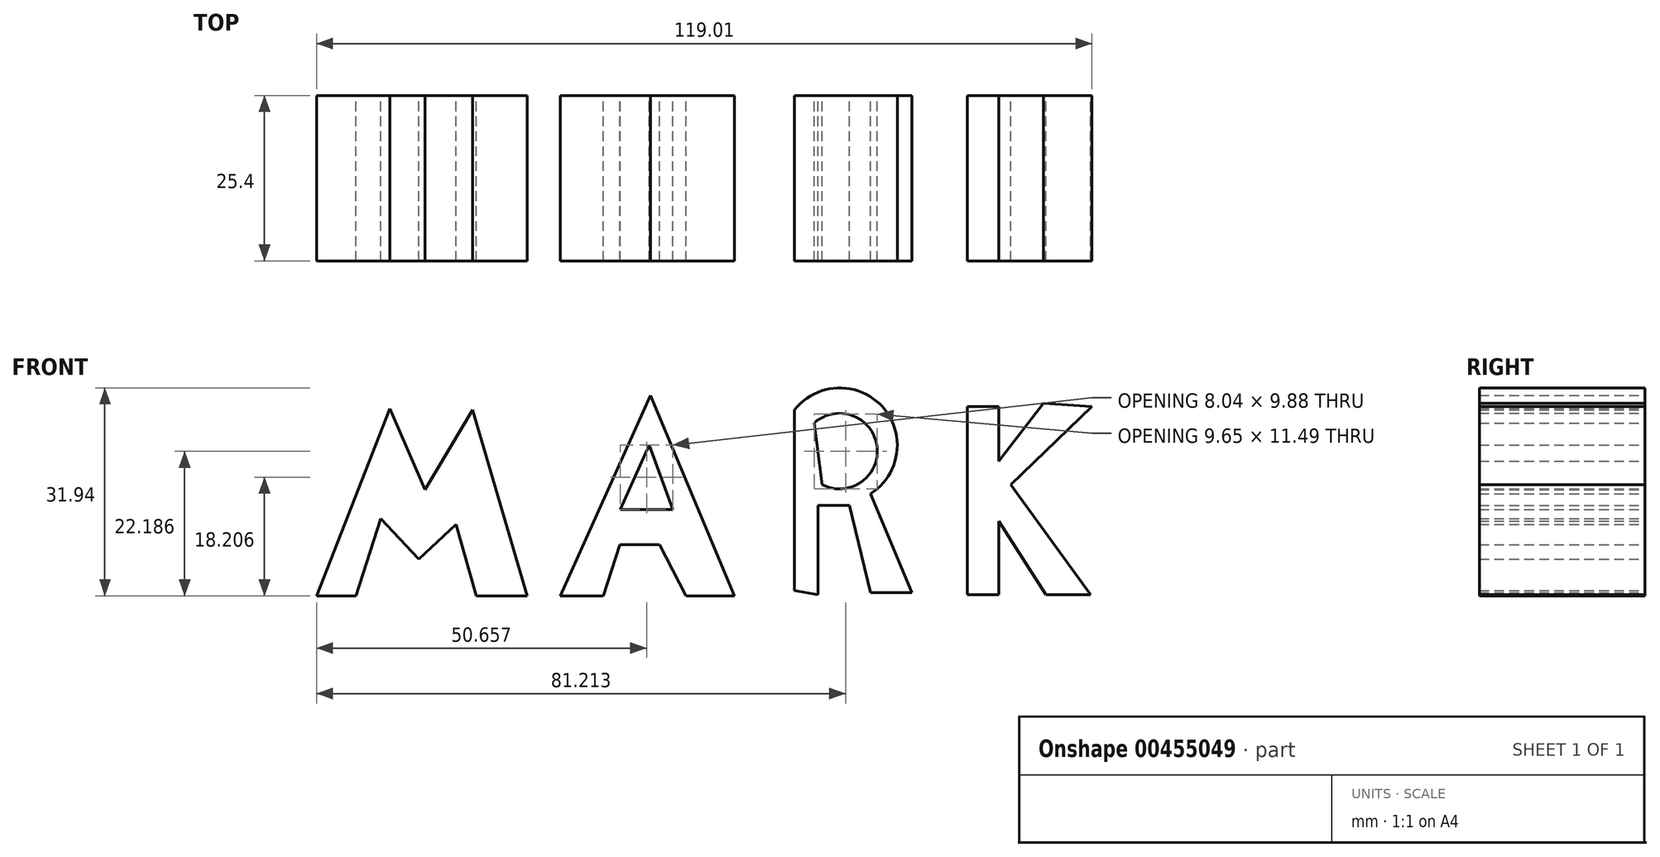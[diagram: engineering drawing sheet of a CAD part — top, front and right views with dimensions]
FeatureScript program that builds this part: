
annotation { "Feature Type Name" : "Feature", "Feature Type Description" : "" }
export const myFeature = defineFeature(function(context is Context, id is Id, definition is map)
    precondition{}
    {
        {
            var Q0;
            Q0=qCreatedBy(makeId("Front.planeOp"),FACE);
            var sketch = newSketch(context, id + "F0", { "sketchPlane" : qUnion([Q0])});
            skLineSegment(sketch, "E0", {"start": v(-68.75, -36.99) * mm, "end": v(-62.72, -36.99) * mm});
            skLineSegment(sketch, "E1", {"start": v(-62.72, -36.99) * mm, "end": v(-58.9, -25.13) * mm});
            skLineSegment(sketch, "E2", {"start": v(-58.9, -25.13) * mm, "end": v(-53.07, -31.36) * mm});
            skLineSegment(sketch, "E3", {"start": v(-53.07, -31.36) * mm, "end": v(-47.36, -26.01) * mm});
            skLineSegment(sketch, "E4", {"start": v(-47.36, -26.01) * mm, "end": v(-44.23, -36.99) * mm});
            skLineSegment(sketch, "E5", {"start": v(-44.23, -36.99) * mm, "end": v(-36.39, -36.99) * mm});
            skLineSegment(sketch, "E6", {"start": v(-36.39, -36.99) * mm, "end": v(-44.83, -8.44) * mm});
            skLineSegment(sketch, "E7", {"start": v(-44.83, -8.44) * mm, "end": v(-52.07, -20.7) * mm});
            skLineSegment(sketch, "E8", {"start": v(-52.07, -20.7) * mm, "end": v(-57.5, -8.24) * mm});
            skLineSegment(sketch, "E9", {"start": v(-57.5, -8.24) * mm, "end": v(-68.75, -36.99) * mm});
            skLineSegment(sketch, "E10", {"start": v(-31.36, -36.99) * mm, "end": v(-24.73, -36.99) * mm});
            skPoint(sketch, "E10.startSnap0", {"position": v(-65.74, -36.99) * mm});
            skPoint(sketch, "E10.endSnap0", {"position": v(-65.74, -36.99) * mm});
            skLineSegment(sketch, "E11", {"start": v(-24.73, -36.99) * mm, "end": v(-22.2, -29.14) * mm});
            skLineSegment(sketch, "E12", {"start": v(-22.2, -29.14) * mm, "end": v(-16.08, -29.14) * mm});
            skLineSegment(sketch, "E13", {"start": v(-16.08, -29.14) * mm, "end": v(-12.06, -36.99) * mm});
            skLineSegment(sketch, "E14", {"start": v(-12.06, -36.99) * mm, "end": v(-4.62, -36.99) * mm});
            skLineSegment(sketch, "E15", {"start": v(-4.62, -36.99) * mm, "end": v(-17.49, -6.23) * mm});
            skLineSegment(sketch, "E16", {"start": v(-17.49, -6.23) * mm, "end": v(-31.36, -36.99) * mm});
            skLineSegment(sketch, "E17", {"start": v(-19.14, -23.72) * mm, "end": v(-14.07, -23.72) * mm});
            skPoint(sketch, "E17.startSnap0", {"position": v(-19.14, -29.14) * mm});
            skPoint(sketch, "E17.endSnap0", {"position": v(-14.07, -33.06) * mm});
            skLineSegment(sketch, "E18", {"start": v(-14.07, -23.72) * mm, "end": v(-22.11, -23.72) * mm});
            skPoint(sketch, "E18.endSnap0", {"position": v(-16.6, -23.72) * mm});
            skLineSegment(sketch, "E19", {"start": v(-22.11, -23.72) * mm, "end": v(-17.66, -13.85) * mm});
            skLineSegment(sketch, "E20", {"start": v(-17.66, -13.85) * mm, "end": v(-14.07, -23.72) * mm});
            skLineSegment(sketch, "E21", {"start": v(4.62, -8.44) * mm, "end": v(4.62, -36.19) * mm});
            skArc(sketch, "E22", {"start": v(16.28, -21.3) * mm, "mid": v(18.1, -7.94) * mm, "end": v(4.62, -8.44) * mm});
            skArc(sketch, "E23", {"start": v(8.85, -19.9) * mm, "mid": v(17.29, -14.02) * mm, "end": v(7.64, -10.45) * mm});
            skLineSegment(sketch, "E24", {"start": v(16.28, -21.3) * mm, "end": v(22.63, -36.47) * mm});
            skLineSegment(sketch, "E25", {"start": v(22.63, -36.47) * mm, "end": v(16.28, -36.47) * mm});
            skLineSegment(sketch, "E26", {"start": v(16.28, -36.47) * mm, "end": v(13.07, -23.12) * mm});
            skLineSegment(sketch, "E27", {"start": v(13.07, -23.12) * mm, "end": v(8.24, -23.12) * mm});
            skLineSegment(sketch, "E28", {"start": v(8.24, -23.12) * mm, "end": v(8.24, -36.79) * mm});
            skLineSegment(sketch, "E29", {"start": v(8.24, -36.79) * mm, "end": v(4.62, -36.19) * mm});
            skLineSegment(sketch, "E30", {"start": v(7.64, -10.45) * mm, "end": v(8.85, -19.9) * mm});
            skLineSegment(sketch, "E31", {"start": v(31.16, -7.94) * mm, "end": v(31.16, -36.79) * mm});
            skPoint(sketch, "E31.startSnap0", {"position": v(18.1, -7.94) * mm});
            skLineSegment(sketch, "E32", {"start": v(31.16, -36.79) * mm, "end": v(35.98, -36.79) * mm});
            skLineSegment(sketch, "E33", {"start": v(35.98, -36.79) * mm, "end": v(35.98, -25.53) * mm});
            skLineSegment(sketch, "E34", {"start": v(35.98, -25.53) * mm, "end": v(43.22, -36.79) * mm});
            skLineSegment(sketch, "E35", {"start": v(43.22, -36.79) * mm, "end": v(50.06, -36.79) * mm});
            skLineSegment(sketch, "E36", {"start": v(50.06, -36.79) * mm, "end": v(37.8, -19.9) * mm});
            skLineSegment(sketch, "E37", {"start": v(37.8, -19.9) * mm, "end": v(50.26, -7.94) * mm});
            skLineSegment(sketch, "E38", {"start": v(50.26, -7.94) * mm, "end": v(42.84, -7.38) * mm});
            skLineSegment(sketch, "E39", {"start": v(42.84, -7.38) * mm, "end": v(35.98, -16.28) * mm});
            skLineSegment(sketch, "E40", {"start": v(35.98, -16.28) * mm, "end": v(35.98, -7.94) * mm});
            skLineSegment(sketch, "E41", {"start": v(35.98, -7.94) * mm, "end": v(31.16, -7.94) * mm});
            skSolve(sketch);
        }
        {
            var Q0;
            Q0=makeQuery(id+"F0.imprint","IMPRINT",FACE,{"disambiguationData":[TD([[makeQuery(id+"F0.imprint","IMPRINT",EDGE,{"derivedFrom":sQuery(id+"F0.wireOp",EDGE,"E0")}),1.0]])]});
            var Q1;
            Q1=makeQuery(id+"F0.imprint","IMPRINT",FACE,{"disambiguationData":[TD([[makeQuery(id+"F0.imprint","IMPRINT",EDGE,{"derivedFrom":sQuery(id+"F0.wireOp",EDGE,"E10")}),1.0]])]});
            var Q2;
            Q2=makeQuery(id+"F0.imprint","IMPRINT",FACE,{"disambiguationData":[TD([[makeQuery(id+"F0.imprint","IMPRINT",EDGE,{"derivedFrom":sQuery(id+"F0.wireOp",EDGE,"E21")}),1.0]])]});
            var Q3;
            Q3=makeQuery(id+"F0.imprint","IMPRINT",FACE,{"disambiguationData":[TD([[makeQuery(id+"F0.imprint","IMPRINT",EDGE,{"derivedFrom":sQuery(id+"F0.wireOp",EDGE,"E31")}),1.0]])]});
            extrude(context, id + "F1", {"entities" : qUnion([Q0, Q1, Q2, Q3]), "depth" : 25.4 * mm});
        }
    });
